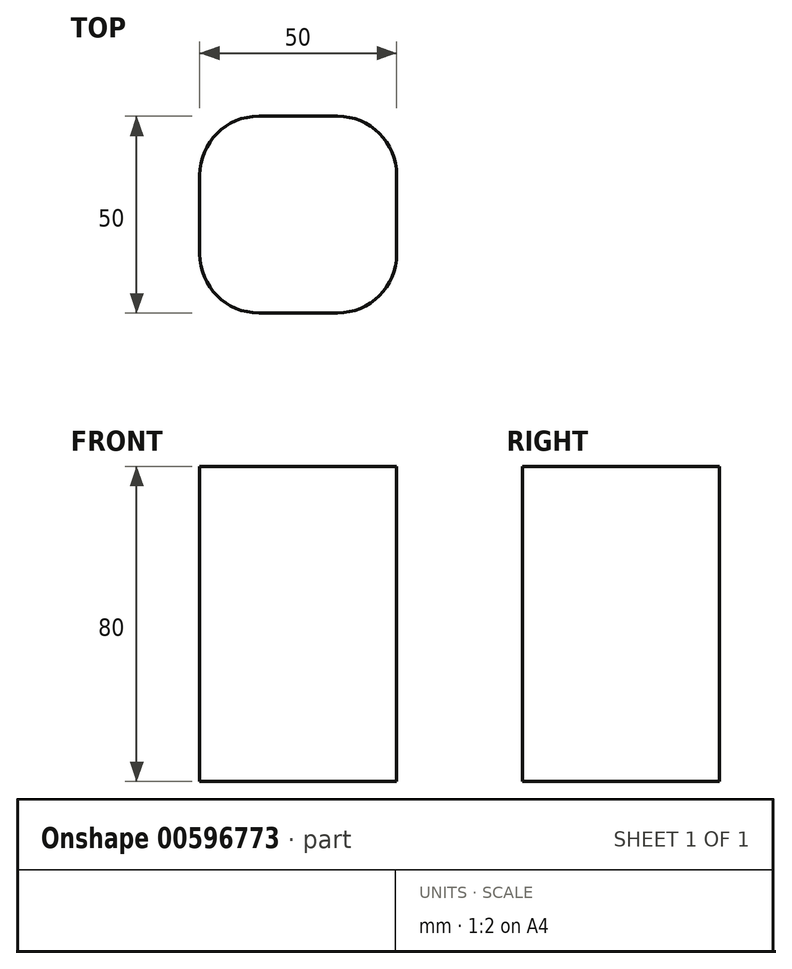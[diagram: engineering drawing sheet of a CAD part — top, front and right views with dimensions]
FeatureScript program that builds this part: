
annotation { "Feature Type Name" : "Feature", "Feature Type Description" : "" }
export const myFeature = defineFeature(function(context is Context, id is Id, definition is map)
    precondition{}
    {
        {
            var Q0;
            Q0=qCreatedBy(makeId("Top.planeOp"),FACE);
            var sketch = newSketch(context, id + "F0", { "sketchPlane" : qUnion([Q0])});
            skLineSegment(sketch, "E0.bottom", {"start": v(25, 25) * mm, "end": v(-25, 25) * mm});
            skLineSegment(sketch, "E0.top", {"start": v(25, -25) * mm, "end": v(-25, -25) * mm});
            skLineSegment(sketch, "E0.left", {"start": v(25, 25) * mm, "end": v(25, -25) * mm});
            skLineSegment(sketch, "E0.right", {"start": v(-25, 25) * mm, "end": v(-25, -25) * mm});
            skPoint(sketch, "E0.middle", {"position": v(0, 0) * mm});
            skSolve(sketch);
        }
        {
            var Q0;
            Q0=makeQuery(id+"F0.imprint","IMPRINT",FACE,{"disambiguationData":[TD([[makeQuery(id+"F0.imprint","IMPRINT",EDGE,{"derivedFrom":sQuery(id+"F0.wireOp",EDGE,"E0.bottom")}),1.0]])]});
            extrude(context, id + "F1", {"entities" : qUnion([Q0]), "depth" : 80 * mm, "offsetDistance" : 25 * mm});
        }
        {
            var Q0;
            Q0=makeQuery(id+"F1.opExtrude","SWEPT_EDGE",EDGE,{"disambiguationData":[OSD([sQuery(id+"F0.wireOp",EDGE,"E0.bottom"),sQuery(id+"F0.wireOp",EDGE,"E0.left")])]});
            var Q1;
            Q1=makeQuery(id+"F1.opExtrude","SWEPT_EDGE",EDGE,{"disambiguationData":[OSD([sQuery(id+"F0.wireOp",EDGE,"E0.top"),sQuery(id+"F0.wireOp",EDGE,"E0.left")])]});
            var Q2;
            Q2=makeQuery(id+"F1.opExtrude","SWEPT_EDGE",EDGE,{"disambiguationData":[OSD([sQuery(id+"F0.wireOp",EDGE,"E0.bottom"),sQuery(id+"F0.wireOp",EDGE,"E0.right")])]});
            var Q3;
            Q3=makeQuery(id+"F1.opExtrude","SWEPT_EDGE",EDGE,{"disambiguationData":[OSD([sQuery(id+"F0.wireOp",EDGE,"E0.top"),sQuery(id+"F0.wireOp",EDGE,"E0.right")])]});
            fillet(context, id + "F2", {"entities" : qUnion([Q0, Q1, Q2, Q3]), "radius" : 15 * mm, "tangentPropagation" : true, "allowEdgeOverflow" : false});
        }
    });
